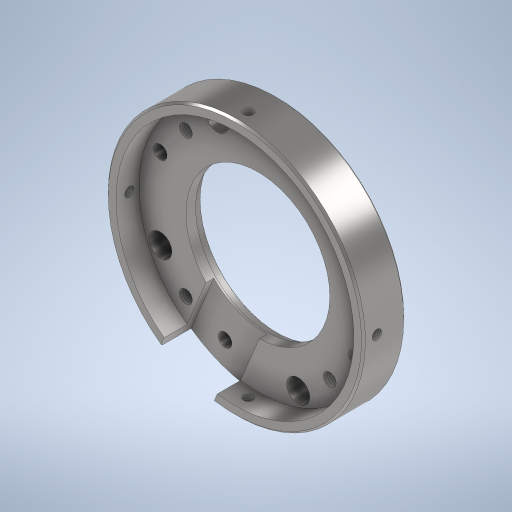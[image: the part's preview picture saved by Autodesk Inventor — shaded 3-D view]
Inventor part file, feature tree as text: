
AUTODESK INVENTOR PART (.ipt)
format: ipt  version: 2023 (Build 270158000, 158)  size: 435,200 bytes
history: native  units: mm
features: sketch x5, hole x4, pattern_circular x2, chamfer x2, plane x2, extrude x2, revolve x1
ambient origin geometry x8: Origin, YZ Plane, XZ Plane, XY Plane, X Axis, Y Axis, Z Axis, Center Point
bodies: Solid1 (feature_tree)
feature tree (18):
  revolve  "Revolution1"  [1 undecoded]
  hole  "Hole1"  [1 undecoded]
  pattern_circular  "Circular Pattern1"  Angle=360.0deg  [1 undecoded]
  hole  "Hole2"  [1 undecoded]
  pattern_circular  "Circular Pattern2"  Count=4 Angle=360.0deg
  chamfer  "Chamfer1"  Distance=55.0mm
  chamfer  "Chamfer2"  Angle=22.5deg  [1 undecoded]
  plane  "Work Plane1"
  plane  "Work Plane2"
  hole  "Hole3"  [1 undecoded]
  hole  "Hole4"  [1 undecoded]
  extrude  "Extrusion1"  Depth=15.0mm
  extrude  "Extrusion3"  Depth=15.0mm
  sketch  "Sketch1"  dims[d0=75.0mm d1=80.0mm]
  sketch  "Sketch4"  dims[d2=5.0mm d3=124.0mm]
  sketch  "Sketch5"  dims[d4=134.0mm]
  sketch  "Sketch6"  dims[d5=12.0mm]
  sketch  "Sketch8"  dims[d8=5.0mm d9=360.0deg d10=53.0mm d11=6.647mm d12=16.0mm d13=4.0mm d14=2.0mm d15=90.0deg d16=22.2mm d17=20.594885mm d18=40.0mm d19=360.0deg d25=55.0mm d30=7.0mm d31=6.0mm d32=12.6mm d33=2.0mm d34=90.0deg d35=8.0mm d36=20.594885mm d37=22.5deg d38=1.0mm d39=2.0mm d40=45.0deg d41=0.2mm d42=2.0mm d43=45.0deg d44=15.0mm d45=4.917mm d46=12.0mm d47=9.4mm d48=2.0mm d49=90.0deg d50=8.0mm d51=20.594885mm d52=15.0mm d53=4.917mm d54=12.0mm d55=4.0mm d56=2.0mm d57=90.0deg d58=8.0mm d59=20.594885mm d60=30.0mm d61=100.0mm d62=16.0mm d63=0.0mm d65=22.5deg d72=45.0deg d73=80.0mm d74=360.0deg d76=12.0mm d77=0.0mm d78=0.0mm d79=15.5mm]
note: 7 required parameter values undecoded (feature->parameter linkage not recoverable at this tier; creation-order binding heuristic only, values carry confidence <= 0.55)